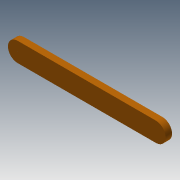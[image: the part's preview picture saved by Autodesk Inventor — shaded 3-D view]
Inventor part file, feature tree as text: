
AUTODESK INVENTOR PART (.ipt)
format: ipt  version: 2013 (Build 170138000, 138)  size: 96,256 bytes
history: native  units: mm
features: extrude x3, sketch x3
ambient origin geometry x8: Origin, YZ Plane, XZ Plane, XY Plane, X Axis, Y Axis, Z Axis, Center Point
bodies: Solid1 (feature_tree)
feature tree (6):
  extrude  "Extrusion1"  Depth=6.0mm
  extrude  "Extrusion2"  Depth=3.0mm
  extrude  "Extrusion3"  Depth=2.0mm TaperAngle=0.0deg
  sketch  "Sketch1"  dims[d0=43.0mm d1=6.0mm]
  sketch  "Sketch2"  dims[d3=2.0mm d4=0.0mm d5=3.0mm]
  sketch  "Sketch3"  dims[d6=3.0mm d7=2.0mm d8=0.0mm d9=0.1mm d10=0.1mm d11=2.0mm d12=0.0mm]
